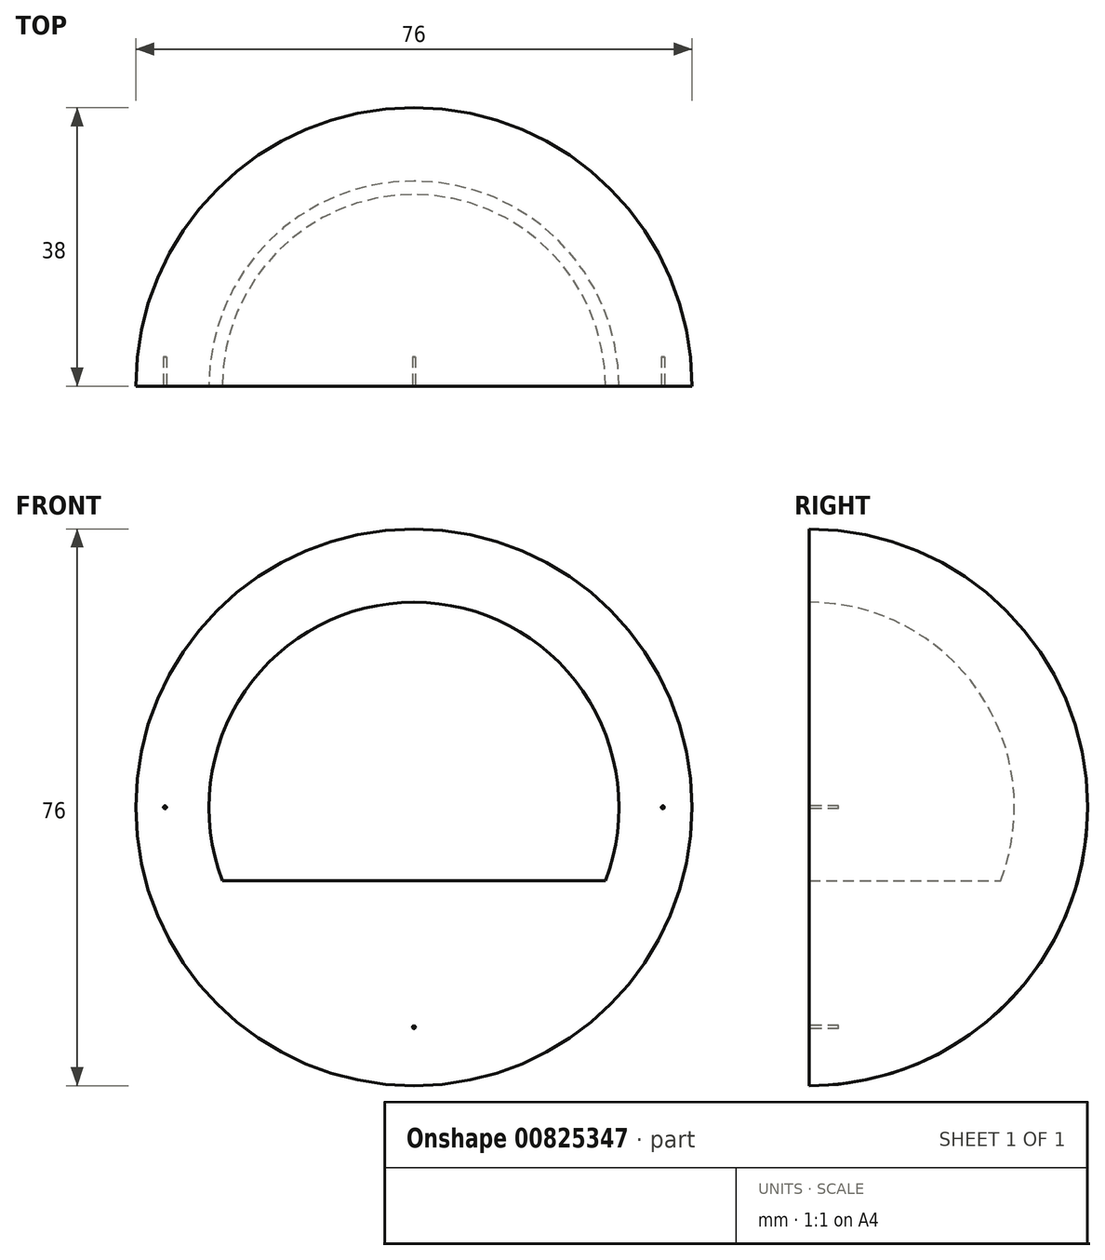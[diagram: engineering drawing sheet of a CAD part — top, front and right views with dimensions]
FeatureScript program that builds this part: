
annotation { "Feature Type Name" : "Feature", "Feature Type Description" : "" }
export const myFeature = defineFeature(function(context is Context, id is Id, definition is map)
    precondition{}
    {
        {
            var Q0;
            Q0=qCreatedBy(makeId("Right.planeOp"),FACE);
            var sketch = newSketch(context, id + "F0", { "sketchPlane" : qUnion([Q0])});
            skArc(sketch, "E0", {"start": v(0, -38) * mm, "mid": v(26.87, -26.87) * mm, "end": v(38, 0) * mm});
            skLineSegment(sketch, "E1", {"start": v(0, -38) * mm, "end": v(0, 0) * mm});
            skLineSegment(sketch, "E2", {"start": v(38, 0) * mm, "end": v(0, 0) * mm});
            skPoint(sketch, "E3.orphan", {"position": v(50.42, 0) * mm});
            skSolve(sketch);
        }
        {
            var Q0;
            Q0=makeQuery(id+"F0.imprint","IMPRINT",FACE,{"disambiguationData":[TD([[makeQuery(id+"F0.imprint","IMPRINT",EDGE,{"derivedFrom":sQuery(id+"F0.wireOp",EDGE,"E0")}),1.0]])]});
            var Q1;
            Q1=sQuery(id+"F0.wireOp",EDGE,"E2");
            revolve(context, id + "F1", {"surfaceOperationType" : NewSurfaceOperationType.NEW, "entities" : qUnion([Q0]), "axis" : qUnion([Q1]), "revolveType" : RevolveType.FULL});
        }
        {
            var Q0;
            Q0=makeQuery(id+"F1.opRevolve","SWEPT_FACE",FACE,{"disambiguationData":[OSD([sQuery(id+"F0.wireOp",EDGE,"E1")])]});
            var sketch = newSketch(context, id + "F2", { "sketchPlane" : qUnion([Q0])});
            skArc(sketch, "E4", {"start": v(0, 28) * mm, "mid": v(-23.07, 15.87) * mm, "end": v(-26.15, -10) * mm});
            skLineSegment(sketch, "E5", {"start": v(-26.15, -10) * mm, "end": v(0, -10) * mm});
            skLineSegment(sketch, "E6", {"start": v(0, 28) * mm, "end": v(0, -10) * mm});
            skPoint(sketch, "E7.orphan", {"position": v(26.15, -10) * mm});
            skSolve(sketch);
        }
        {
            var Q0;
            Q0=makeQuery(id+"F2.imprint","IMPRINT",FACE,{"disambiguationData":[TD([[makeQuery(id+"F2.imprint","IMPRINT",EDGE,{"derivedFrom":sQuery(id+"F2.wireOp",EDGE,"E4")}),1.0]])]});
            var Q1;
            Q1=sQuery(id+"F2.wireOp",EDGE,"E6");
            revolve(context, id + "F3", {"operationType" : NewBodyOperationType.REMOVE, "surfaceOperationType" : NewSurfaceOperationType.NEW, "entities" : qUnion([Q0]), "axis" : qUnion([Q1]), "revolveType" : RevolveType.FULL, "oppositeDirection" : true});
        }
        {
            var Q0;
            Q0=makeQuery(id+"F1.opRevolve","SWEPT_FACE",FACE,{"disambiguationData":[OSD([sQuery(id+"F0.wireOp",EDGE,"E1")])]});
            var sketch = newSketch(context, id + "F4", { "sketchPlane" : qUnion([Q0])});
            skLineSegment(sketch, "E8", {"start": v(0, 38) * mm, "end": v(0, -38) * mm, "construction": true});
            skLineSegment(sketch, "E9", {"start": v(-38, 0) * mm, "end": v(38, 0) * mm, "construction": true});
            skLineSegment(sketch, "E10.0", {"start": v(-38, -30) * mm, "end": v(38, -30) * mm, "construction": true});
            skCircle(sketch, "E11", {"center": v(0, -30) * mm, "radius": 0.2 * mm});
            skCircle(sketch, "E12", {"center": v(34, 0) * mm, "radius": 0.2 * mm});
            skCircle(sketch, "E13.MirrorC", {"center": v(-34, 0) * mm, "radius": 0.2 * mm});
            skSolve(sketch);
        }
        {
            var Q0;
            Q0 = qSketchRegion(id + "F4", true);
            extrude(context, id + "F5", {"entities" : qUnion([Q0]), "operationType" : NewBodyOperationType.REMOVE, "oppositeDirection" : true, "depth" : 4 * mm, "offsetDistance" : 25 * mm});
        }
    });
